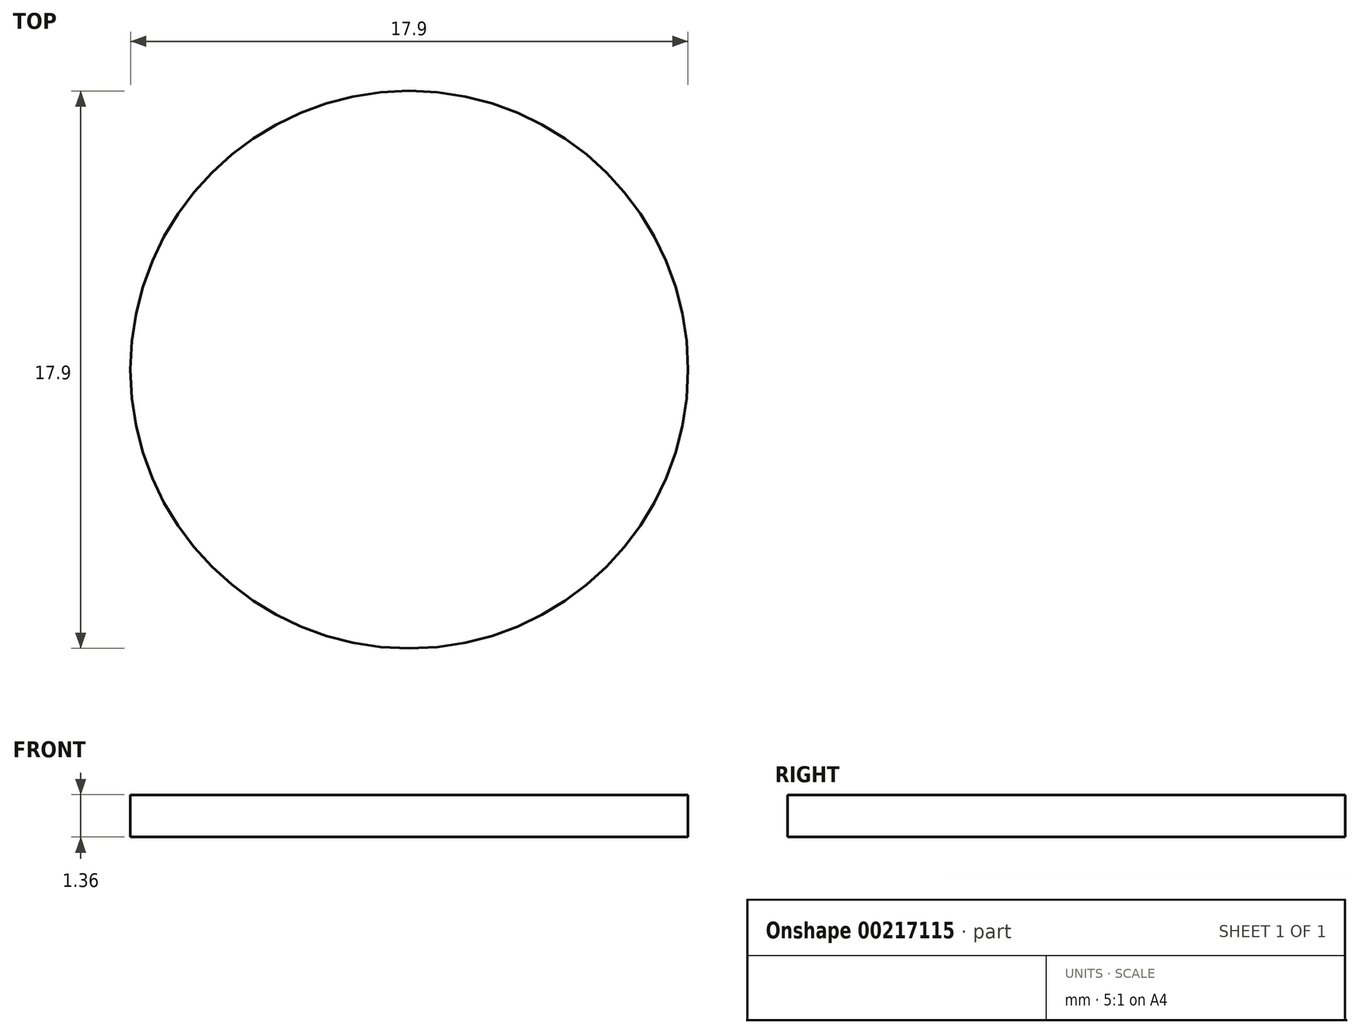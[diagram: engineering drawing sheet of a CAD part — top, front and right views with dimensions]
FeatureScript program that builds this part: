
annotation { "Feature Type Name" : "Feature", "Feature Type Description" : "" }
export const myFeature = defineFeature(function(context is Context, id is Id, definition is map)
    precondition{}
    {
        {
            var Q0;
            Q0=qCreatedBy(makeId("Top.planeOp"),FACE);
            var sketch = newSketch(context, id + "F0", { "sketchPlane" : qUnion([Q0])});
            skCircle(sketch, "E0", {"center": v(0, 0) * mm, "radius": 8.95 * mm});
            skSolve(sketch);
        }
        {
            var Q0;
            Q0 = qSketchRegion(id + "F0", true);
            extrude(context, id + "F1", {"entities" : qUnion([Q0]), "endBound" : BoundingType.SYMMETRIC, "depth" : 1.35 * mm});
        }
    });
